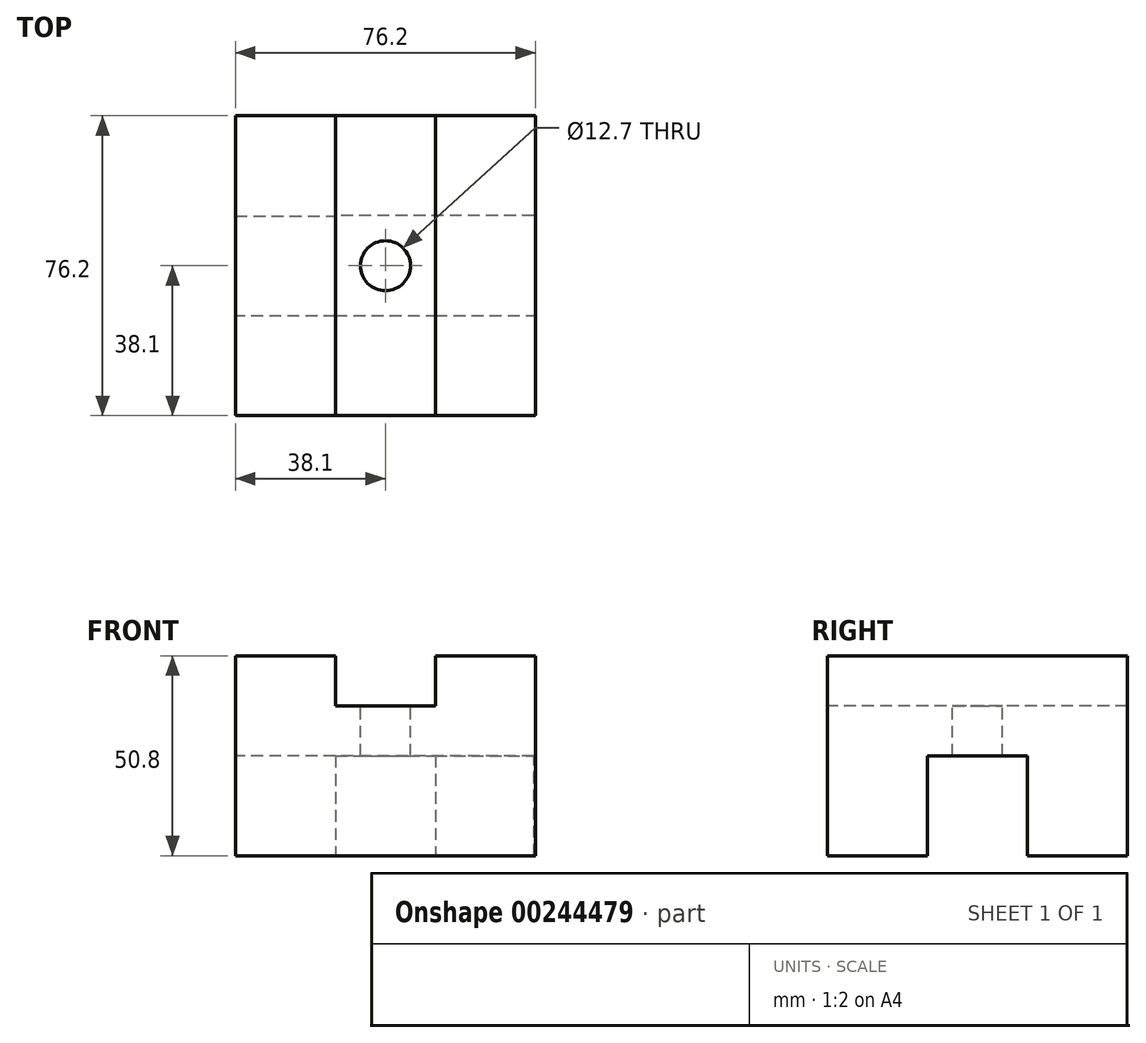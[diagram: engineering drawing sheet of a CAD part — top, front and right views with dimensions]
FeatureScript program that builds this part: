
annotation { "Feature Type Name" : "Feature", "Feature Type Description" : "" }
export const myFeature = defineFeature(function(context is Context, id is Id, definition is map)
    precondition{}
    {
        {
            var Q0;
            Q0=qCreatedBy(makeId("Top.planeOp"),FACE);
            var sketch = newSketch(context, id + "F0", { "sketchPlane" : qUnion([Q0])});
            skLineSegment(sketch, "E0.bottom", {"start": v(-38.1, 38.1) * mm, "end": v(38.1, 38.1) * mm});
            skLineSegment(sketch, "E0.top", {"start": v(-38.1, -38.1) * mm, "end": v(38.1, -38.1) * mm});
            skLineSegment(sketch, "E0.left", {"start": v(-38.1, 38.1) * mm, "end": v(-38.1, -38.1) * mm});
            skLineSegment(sketch, "E0.right", {"start": v(38.1, 38.1) * mm, "end": v(38.1, -38.1) * mm});
            skPoint(sketch, "E0.middle", {"position": v(0, 0) * mm});
            skSolve(sketch);
        }
        {
            var Q0;
            Q0 = qSketchRegion(id + "F0", true);
            extrude(context, id + "F1", {"entities" : qUnion([Q0]), "depth" : 50.8 * mm});
        }
        {
            var Q0;
            Q0=makeQuery(id+"F1.opExtrude","CAP_FACE",FACE,{"disambiguationData":[OSD([sQuery(id+"F0.wireOp",EDGE,"E0.bottom"),sQuery(id+"F0.wireOp",EDGE,"E0.top"),sQuery(id+"F0.wireOp",EDGE,"E0.left"),sQuery(id+"F0.wireOp",EDGE,"E0.right")])],"isStart":false});
            var sketch = newSketch(context, id + "F2", { "sketchPlane" : qUnion([Q0])});
            skLineSegment(sketch, "E1", {"start": v(38.1, 38.1) * mm, "end": v(12.7, 38.1) * mm});
            skLineSegment(sketch, "E2", {"start": v(12.7, 38.1) * mm, "end": v(12.7, -38.1) * mm});
            skLineSegment(sketch, "E3", {"start": v(12.7, -38.1) * mm, "end": v(-12.7, -38.1) * mm});
            skLineSegment(sketch, "E4", {"start": v(-12.7, -38.1) * mm, "end": v(-12.7, 38.1) * mm});
            skLineSegment(sketch, "E5", {"start": v(-12.7, 38.1) * mm, "end": v(-38.1, 38.1) * mm});
            skLineSegment(sketch, "E6", {"start": v(-38.1, 38.1) * mm, "end": v(-38.1, -38.1) * mm});
            skLineSegment(sketch, "E7", {"start": v(12.7, 38.1) * mm, "end": v(-12.7, 38.1) * mm});
            skLineSegment(sketch, "E8", {"start": v(12.7, -38.1) * mm, "end": v(38.1, -38.1) * mm});
            skLineSegment(sketch, "E9", {"start": v(38.1, -38.1) * mm, "end": v(38.1, 38.1) * mm});
            skSolve(sketch);
        }
        {
            var Q0;
            Q0=makeQuery(id+"F2.imprint","IMPRINT",FACE,{"disambiguationData":[TD([[makeQuery(id+"F2.imprint","IMPRINT",EDGE,{"derivedFrom":sQuery(id+"F2.wireOp",EDGE,"E2")}),-1.0]])]});
            extrude(context, id + "F3", {"entities" : qUnion([Q0]), "operationType" : NewBodyOperationType.REMOVE, "oppositeDirection" : true, "depth" : 12.7 * mm});
        }
        {
            var Q0;
            Q0=makeQuery(id+"F1.opExtrude","CAP_FACE",FACE,{"disambiguationData":[OSD([sQuery(id+"F0.wireOp",EDGE,"E0.bottom"),sQuery(id+"F0.wireOp",EDGE,"E0.top"),sQuery(id+"F0.wireOp",EDGE,"E0.left"),sQuery(id+"F0.wireOp",EDGE,"E0.right")])],"isStart":true});
            var sketch = newSketch(context, id + "F4", { "sketchPlane" : qUnion([Q0])});
            skLineSegment(sketch, "E10", {"start": v(-38.1, 38.1) * mm, "end": v(-38.1, -38.1) * mm});
            skLineSegment(sketch, "E11", {"start": v(-38.1, -38.1) * mm, "end": v(-12.7, -38.1) * mm});
            skLineSegment(sketch, "E12", {"start": v(-12.7, -38.1) * mm, "end": v(-12.7, 38.1) * mm});
            skLineSegment(sketch, "E13", {"start": v(-38.1, 38.1) * mm, "end": v(-12.7, 38.1) * mm});
            skLineSegment(sketch, "E14", {"start": v(-12.7, 38.1) * mm, "end": v(12.7, 38.1) * mm});
            skLineSegment(sketch, "E15", {"start": v(12.7, 38.1) * mm, "end": v(12.7, -38.1) * mm});
            skLineSegment(sketch, "E16", {"start": v(12.7, -38.1) * mm, "end": v(-12.7, -38.1) * mm});
            skLineSegment(sketch, "E17", {"start": v(12.7, -38.1) * mm, "end": v(38.1, -38.1) * mm});
            skLineSegment(sketch, "E18", {"start": v(38.1, -38.1) * mm, "end": v(38.1, 38.1) * mm});
            skLineSegment(sketch, "E19", {"start": v(38.1, 38.1) * mm, "end": v(12.7, 38.1) * mm});
            skSolve(sketch);
        }
        {
            var Q0;
            Q0=makeQuery(id+"F4.imprint","IMPRINT",FACE,{"disambiguationData":[TD([[makeQuery(id+"F4.imprint","IMPRINT",EDGE,{"derivedFrom":sQuery(id+"F4.wireOp",EDGE,"E10")}),-1.0]])]});
            var sketch = newSketch(context, id + "F5", { "sketchPlane" : qUnion([Q0])});
            skLineSegment(sketch, "E20", {"start": v(-38.45, -38.15) * mm, "end": v(-38.45, -12.75) * mm});
            skLineSegment(sketch, "E21", {"start": v(-38.45, -38.15) * mm, "end": v(37.75, -38.15) * mm});
            skLineSegment(sketch, "E22", {"start": v(37.75, -38.15) * mm, "end": v(37.75, -12.75) * mm});
            skLineSegment(sketch, "E23", {"start": v(37.75, -12.75) * mm, "end": v(-38.45, -12.75) * mm});
            skLineSegment(sketch, "E24", {"start": v(-38.45, -12.75) * mm, "end": v(-38.45, 12.65) * mm});
            skLineSegment(sketch, "E25", {"start": v(-38.45, 12.65) * mm, "end": v(37.75, 12.65) * mm});
            skLineSegment(sketch, "E26", {"start": v(37.75, 12.65) * mm, "end": v(37.75, -12.75) * mm});
            skLineSegment(sketch, "E27", {"start": v(37.75, 12.65) * mm, "end": v(37.75, 38.05) * mm});
            skLineSegment(sketch, "E28", {"start": v(37.75, 38.05) * mm, "end": v(-38.45, 38.05) * mm});
            skLineSegment(sketch, "E29", {"start": v(-38.45, 38.05) * mm, "end": v(-38.45, 12.65) * mm});
            skSolve(sketch);
        }
        {
            var Q0;
            Q0=makeQuery(id+"F4.imprint","IMPRINT",FACE,{"disambiguationData":[TD([[makeQuery(id+"F4.imprint","IMPRINT",EDGE,{"derivedFrom":sQuery(id+"F4.wireOp",EDGE,"E12")}),-1.0]])]});
            var sketch = newSketch(context, id + "F6", { "sketchPlane" : qUnion([Q0])});
            skLineSegment(sketch, "E30", {"start": v(37.35, 38.14) * mm, "end": v(-38.85, 38.14) * mm});
            skLineSegment(sketch, "E31", {"start": v(37.35, 38.14) * mm, "end": v(37.35, 12.74) * mm});
            skLineSegment(sketch, "E32", {"start": v(37.35, 12.74) * mm, "end": v(-38.85, 12.74) * mm});
            skLineSegment(sketch, "E33", {"start": v(-38.85, 12.74) * mm, "end": v(-38.85, -12.66) * mm});
            skLineSegment(sketch, "E34", {"start": v(-38.85, -12.66) * mm, "end": v(37.35, -12.66) * mm});
            skLineSegment(sketch, "E35", {"start": v(37.35, -12.66) * mm, "end": v(37.35, 12.74) * mm});
            skLineSegment(sketch, "E36", {"start": v(37.35, -12.66) * mm, "end": v(37.35, -38.06) * mm});
            skLineSegment(sketch, "E37", {"start": v(37.35, -38.06) * mm, "end": v(-38.85, -38.06) * mm});
            skLineSegment(sketch, "E38", {"start": v(-38.85, -38.06) * mm, "end": v(-38.85, -12.66) * mm});
            skLineSegment(sketch, "E39", {"start": v(-38.85, 12.74) * mm, "end": v(-38.85, 38.14) * mm});
            skSolve(sketch);
        }
        {
            var Q0;
            {var subQ0=sQuery(id+"F6.wireOp",EDGE,"E33");Q0=makeQuery(id+"F6.imprint","IMPRINT",FACE,{"disambiguationData":[TD([[makeQuery(id+"F6.imprint","IMPRINT",EDGE,{"derivedFrom":subQ0}),1.0]])]});}
            extrude(context, id + "F7", {"entities" : qUnion([Q0]), "operationType" : NewBodyOperationType.REMOVE, "oppositeDirection" : true, "depth" : 25.4 * mm});
        }
        {
            var Q0;
            {var subQ0=sQuery(id+"F5.wireOp",EDGE,"E26");Q0=makeQuery(id+"F5.imprint","IMPRINT",FACE,{"disambiguationData":[TD([[makeQuery(id+"F5.imprint","IMPRINT",EDGE,{"derivedFrom":subQ0}),-1.0]])]});}
            extrude(context, id + "F8", {"entities" : qUnion([Q0]), "operationType" : NewBodyOperationType.REMOVE, "oppositeDirection" : true, "depth" : 25.4 * mm});
        }
        {
            var Q0;
            Q0=makeQuery(id+"F1.opExtrude","SWEPT_FACE",FACE,{"disambiguationData":[OSD([sQuery(id+"F0.wireOp",EDGE,"E0.right")])]});
            var sketch = newSketch(context, id + "F9", { "sketchPlane" : qUnion([Q0])});
            skLineSegment(sketch, "E40", {"start": v(38.1, 0) * mm, "end": v(12.7, 0) * mm});
            skLineSegment(sketch, "E41", {"start": v(12.7, 0) * mm, "end": v(-12.7, 0) * mm});
            skLineSegment(sketch, "E42", {"start": v(-12.7, 0) * mm, "end": v(-12.7, 12.7) * mm});
            skLineSegment(sketch, "E43", {"start": v(-12.7, 12.7) * mm, "end": v(12.7, 12.7) * mm});
            skLineSegment(sketch, "E44", {"start": v(12.7, 12.7) * mm, "end": v(12.7, 0) * mm});
            skSolve(sketch);
        }
        {
            var Q0;
            Q0=makeQuery(id+"F9.imprint","IMPRINT",FACE,{"disambiguationData":[TD([[makeQuery(id+"F9.imprint","IMPRINT",EDGE,{"derivedFrom":sQuery(id+"F9.wireOp",EDGE,"E41")}),-1.0]])]});
            extrude(context, id + "F10", {"entities" : qUnion([Q0]), "operationType" : NewBodyOperationType.REMOVE, "oppositeDirection" : true, "depth" : 25.4 * mm});
        }
        {
            var Q0;
            Q0=makeQuery(id+"F1.opExtrude","SWEPT_FACE",FACE,{"disambiguationData":[OSD([sQuery(id+"F0.wireOp",EDGE,"E0.right")])]});
            var sketch = newSketch(context, id + "F11", { "sketchPlane" : qUnion([Q0])});
            skLineSegment(sketch, "E45", {"start": v(-12.7, 12.7) * mm, "end": v(-12.7, 25.4) * mm});
            skLineSegment(sketch, "E46", {"start": v(-12.7, 25.4) * mm, "end": v(12.7, 25.4) * mm});
            skLineSegment(sketch, "E47", {"start": v(12.7, 25.4) * mm, "end": v(12.7, 12.7) * mm});
            skSolve(sketch);
        }
        {
            var Q0;
            Q0=makeQuery(id+"F11.imprint","IMPRINT",FACE,{"disambiguationData":[TD([[makeQuery(id+"F11.imprint","IMPRINT",EDGE,{"derivedFrom":sQuery(id+"F11.wireOp",EDGE,"E45")}),-1.0]])]});
            extrude(context, id + "F12", {"entities" : qUnion([Q0]), "operationType" : NewBodyOperationType.REMOVE, "oppositeDirection" : true, "depth" : 25.4 * mm});
        }
        {
            var Q0;
            Q0=makeQuery(id+"F3.boolean.opBoolean","COPY",FACE,{"derivedFrom":makeQuery(id+"F3.opExtrude","CAP_FACE",FACE,{"disambiguationData":[OSD([sQuery(id+"F2.wireOp",EDGE,"E2"),sQuery(id+"F2.wireOp",EDGE,"E3"),sQuery(id+"F2.wireOp",EDGE,"E4"),sQuery(id+"F2.wireOp",EDGE,"E7")])],"isStart":false})});
            var sketch = newSketch(context, id + "F13", { "sketchPlane" : qUnion([Q0])});
            skPoint(sketch, "E48", {"position": v(0, 0) * mm});
            skSolve(sketch);
        }
        {
            var Q0;
            Q0=sQuery(id+"F13.wireOp",VERTEX,"E48");
            var Q1;
            Q1=makeQuery(id+"F1.opExtrude","SWEPT_BODY",BODY,{"disambiguationData":[OSD([sQuery(id+"F0.wireOp",EDGE,"E0.bottom"),sQuery(id+"F0.wireOp",EDGE,"E0.top"),sQuery(id+"F0.wireOp",EDGE,"E0.left"),sQuery(id+"F0.wireOp",EDGE,"E0.right")])]});
            hole(context, id + "F14", {"style" : HoleStyle.SIMPLE, "endStyle" : HoleEndStyle.THROUGH, "holeDiameter" : 12.7 * mm, "tappedDepth" : 12.7 * mm, "tapClearance" : 3, "locations" : qUnion([Q0]), "scope" : qUnion([Q1])});
        }
    });
